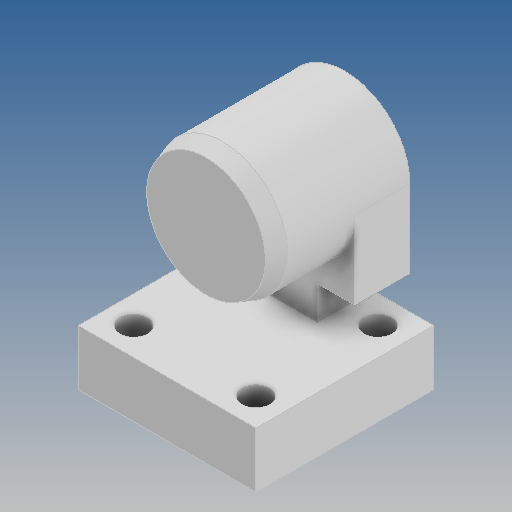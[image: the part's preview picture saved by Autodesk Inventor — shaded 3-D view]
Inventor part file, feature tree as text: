
AUTODESK INVENTOR PART (.ipt)
format: ipt  version: 2020 (Build 240168000, 168)  size: 172,544 bytes
history: native  units: mm
features: sketch x5, extrude x4, hole x1, chamfer x1, projected_geometry x1
ambient origin geometry x8: Origin, YZ Plane, XZ Plane, XY Plane, X Axis, Y Axis, Z Axis, Center Point
bodies: Solid1 (feature_tree)
feature tree (12):
  extrude  "Extrusion1"  Depth=15.0mm TaperAngle=0.0deg
  extrude  "Extrusion2"  Depth=10.0mm TaperAngle=0.0deg
  extrude  "Extrusion3"  Depth=32.0mm
  hole  "Hole1"  [1 undecoded]
  extrude  "Extrusion4"  Depth=10.0mm
  chamfer  "Chamfer1"  Distance=6.0mm
  sketch  "Sketch1"  dims[d0=23.4mm d1=15.0mm d2=0.0mm]
  sketch  "Sketch2"  dims[d3=20.0mm d4=10.0mm d5=0.0mm]
  projected_geometry  "Projected Loop1"
  sketch  "Sketch3"  dims[d6=32.0mm d7=32.0mm]
  sketch  "Sketch4"  dims[d8=10.0mm d9=0.0mm d10=22.0mm]
  sketch  "Sketch5"  dims[d11=22.0mm d12=5.0mm d13=10.0mm d14=4.0mm d15=2.0mm d16=90.0deg d17=8.0mm d18=20.594885mm d19=10.0mm d20=6.0mm d21=19.0mm d22=0.0mm d23=1.0mm d24=3.0mm d25=45.0deg]
note: 1 required parameter value undecoded (feature->parameter linkage not recoverable at this tier; creation-order binding heuristic only, values carry confidence <= 0.55)
